# Revit family: FantiniCosmi_BIM_AP20052
name_source: partatom
category: Modelli generici
units: mm (PartAtom-declared; Revit-internal decimal feet)

## family parameters
Basato su piano di lavoro = No
Condiviso = No
Punto di calcolo locali = No
Può ospitare armatura = No
Quota connettore circolare = Usa diametro
Sempre verticale = Sì
Taglio con vuoti quando caricato = No
Tipo di parte = Normale

## types (1)
- Standard
    Area = 9,42 m²
    Average Sound Pressure (Lp) 1Mt = 42.1 dB(A)
    Average Sound Pressure (Lp) 3Mt = 34.7 dB(A)
    Descrizione = HRP DOMO 10 Z
    Fan Number = 2
    Filteration Class = ePM1  80%
    Heat Recovery Efficiency = 85.2 %
    Max Flow = 200 mc/h
    Part Number = FantiniCosmi_BIM_AP20052
    Pressure = 100 Pa
    Prospetto di default = 0 mm  [stored 0 ft]
    Sound Power (Lw) from body = 49 dB(A)
    Sound Power (Lw) from channels = 54 dB(A)

note: [stored X ft] marks values corroborated as IEEE doubles in the binary element streams (Revit-internal decimal feet)

## geometry (parser evidence)
native form markers: Sweep x3
no freeform markers — native parametric forms only
